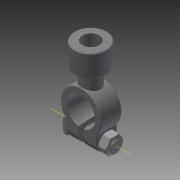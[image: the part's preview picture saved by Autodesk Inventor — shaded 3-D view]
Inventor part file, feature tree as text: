
AUTODESK INVENTOR PART (.ipt)
format: ipt  version: 2014 (Build 180170000, 170)  size: 487,424 bytes
history: native  units: in
note: dims shown in document units (in); Inventor stores cm internally (conversion verified against a paired STEP export)
features: sketch x11, projected_geometry x10, plane x8, extrude x7, fillet x7, other x3, revolve x2, hole x1, thread x1, chamfer x1, surface_op x1, mirror x1, reference x1
ambient origin geometry x8: Origin, YZ Plane, XZ Plane, XY Plane, X Axis, Y Axis, Z Axis, Center Point
bodies: Solid1 (feature_tree), Solid3 (feature_tree), Solid5 (feature_tree)
feature tree (54):
  extrude  "Extrusion1"  Depth=0.125in
  fillet  "Fillet1"  Radius=0.5in
  hole  "Hole1"  [1 undecoded]
  plane  "Work Plane1"
  extrude  "Extrusion6"  Depth=0.15in TaperAngle=0.0deg
  plane  "Work Plane2"
  sketch  "Sketch8"  dims[d19=0.0625in d28=0.15in d29=0.0in]
  other  "Work Axis1"
  revolve  "Revolution2"  [1 undecoded]
  fillet  "Fillet2"  Radius=0.01in
  fillet  "Fillet3"  Radius=0.2in
  extrude  "Extrusion7"  Depth=0.035in
  plane  "Work Plane3"
  revolve  "Revolution3"  [1 undecoded]
  plane  "Work Plane5"
  extrude  "Extrusion8"  Depth=0.125in
  thread  "Thread1"  [1 undecoded]
  chamfer  "Chamfer1"  Distance=0.75in
  plane  "Work Plane7"
  plane  "Work Plane8"
  fillet  "Fillet6"  Radius=0.75in
  fillet  "Fillet7"  Radius=0.5625in
  surface_op  "Sculpt1"
  plane  "Work Plane9"
  mirror  "Mirror3"
  plane  "Work Plane10"
  extrude  "Extrusion11"  Depth=0.035in TaperAngle=0.0deg
  extrude  "Extrusion12"  Depth=0.035in
  extrude  "Extrusion13"  Depth=0.035in
  fillet  "Fillet9"  [1 undecoded]
  fillet  "Fillet10"  [1 undecoded]
  sketch  "Sketch1"  dims[d0=0.15in d1=0.125in d7=0.5in d8=0.0in]
  reference  "Reference1"
  sketch  "Sketch2"  dims[d9=0.2in]
  projected_geometry  "Projected Loop1"
  sketch  "Sketch7"  dims[d10=0.25in d11=0.75in d12=0.375in d13=0.25in d14=0.5635in d15=1.0in d16=0.8108in d17=0.315in]
  projected_geometry  "Projected Loop5"
  sketch  "Sketch9"  dims[d30=90.0deg d31=0.02in d32=0.01in d33=0.2in d34=0.0in]
  projected_geometry  "Projected Loop6"
  projected_geometry  "Projected Loop7"
  sketch  "Sketch10"  dims[d35=90.0deg d36=0.035in]
  sketch  "Sketch11"  dims[d37=0.2in d38=0.0in d39=1.0in d40=0.0in]
  projected_geometry  "Projected Loop8"
  projected_geometry  "Projected Loop9"
  sketch  "Sketch12"  dims[d41=0.02in d42=0.125in d43=45.0deg d53=0.0625in d58=0.1in]
  sketch  "Sketch16"  dims[d59=0.02in]
  projected_geometry  "Projected Loop12"
  sketch  "Sketch17"  dims[d61=0.8125in]
  projected_geometry  "Projected Loop13"
  sketch  "Sketch18"  dims[d62=0.0625in d63=0.75in d64=0.0in d65=0.75in d66=0.5625in d67=0.0172in d68=0.1in d69=0.0in d70=0.035in d71=0.035in]
  projected_geometry  "Projected Loop14"
  projected_geometry  "Project Cut Edges1"
  other  "Composite1"
  other  "Srf1"
note: 6 required parameter values undecoded (feature->parameter linkage not recoverable at this tier; creation-order binding heuristic only, values carry confidence <= 0.55)